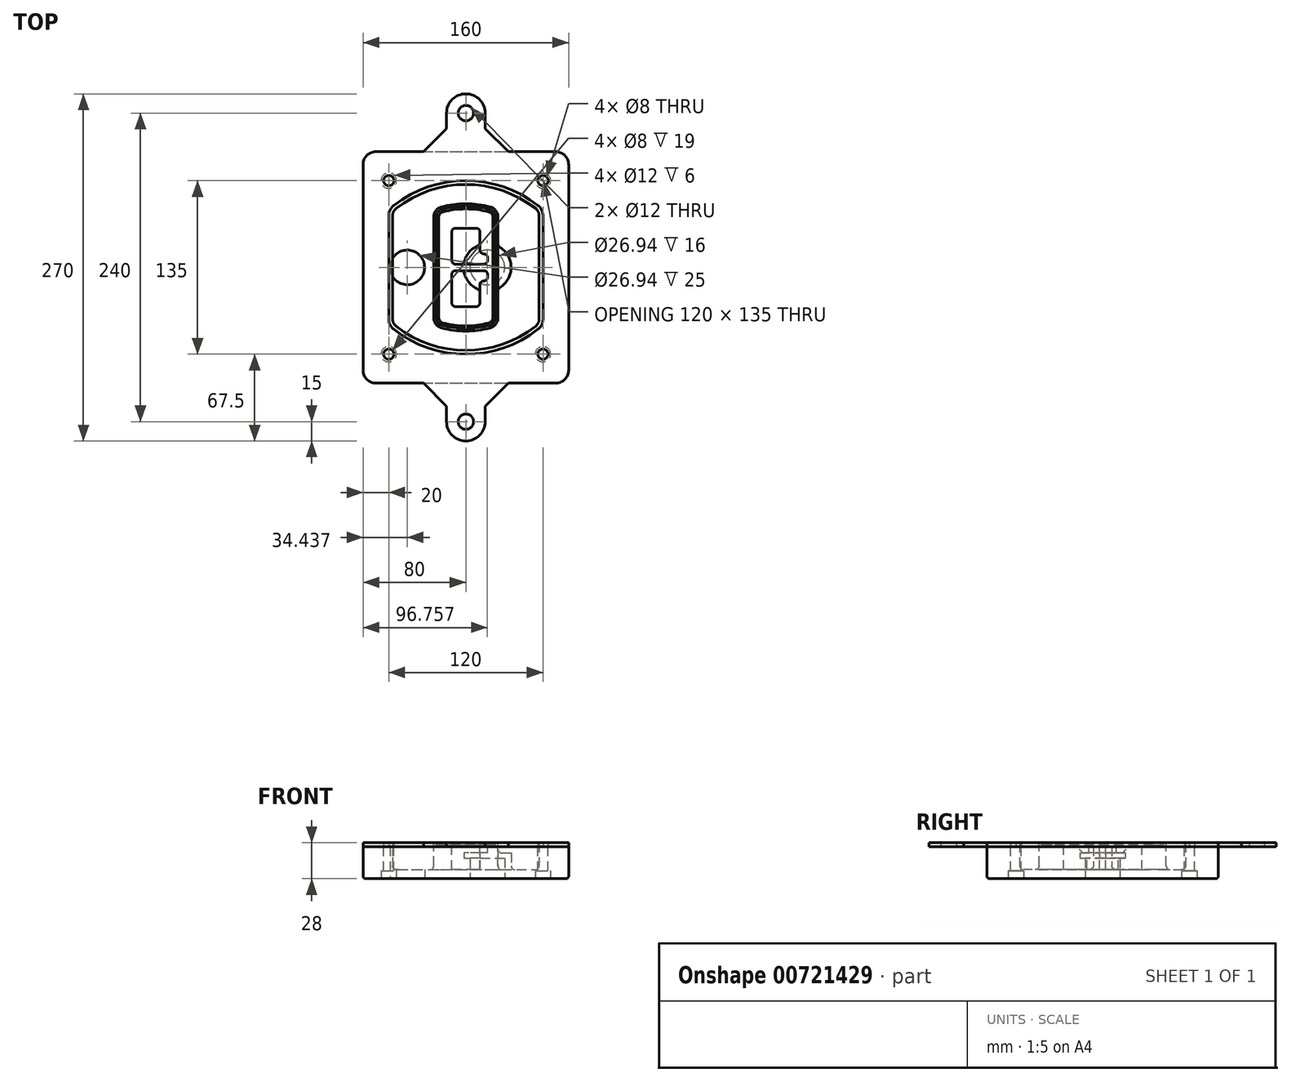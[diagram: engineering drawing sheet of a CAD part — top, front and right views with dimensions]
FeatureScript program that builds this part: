
annotation { "Feature Type Name" : "Feature", "Feature Type Description" : "" }
export const myFeature = defineFeature(function(context is Context, id is Id, definition is map)
    precondition{}
    {
        {
            var Q0;
            Q0=qCreatedBy(makeId("Top.planeOp"),FACE);
            var sketch = newSketch(context, id + "F0", { "sketchPlane" : qUnion([Q0])});
            skPoint(sketch, "E0.rect.middle", {"position": v(0, 0) * mm});
            skLineSegment(sketch, "E1.bottom", {"start": v(-70, -90) * mm, "end": v(70, -90) * mm});
            skLineSegment(sketch, "E1.top", {"start": v(-70, 90) * mm, "end": v(70, 90) * mm});
            skLineSegment(sketch, "E1.left", {"start": v(-80, -80) * mm, "end": v(-80, 80) * mm});
            skLineSegment(sketch, "E1.right", {"start": v(80, -80) * mm, "end": v(80, 80) * mm});
            skLineSegment(sketch, "E2", {"start": v(-80, 90) * mm, "end": v(80, -90) * mm, "construction": true});
            skLineSegment(sketch, "E3", {"start": v(80, 90) * mm, "end": v(-80, -90) * mm, "construction": true});
            skCircle(sketch, "E4", {"center": v(-60, 67.5) * mm, "radius": 4 * mm});
            skCircle(sketch, "E5", {"center": v(60, 67.5) * mm, "radius": 4 * mm});
            skCircle(sketch, "E6", {"center": v(60, -67.5) * mm, "radius": 4 * mm});
            skCircle(sketch, "E7", {"center": v(-60, -67.5) * mm, "radius": 4 * mm});
            skLineSegment(sketch, "E8", {"start": v(-60, 67.5) * mm, "end": v(60, 67.5) * mm, "construction": true});
            skLineSegment(sketch, "E9", {"start": v(60, 67.5) * mm, "end": v(60, -67.5) * mm, "construction": true});
            skLineSegment(sketch, "E10", {"start": v(60, -67.5) * mm, "end": v(-60, -67.5) * mm, "construction": true});
            skLineSegment(sketch, "E11", {"start": v(-60, -67.5) * mm, "end": v(-60, 67.5) * mm, "construction": true});
            skLineSegment(sketch, "E12", {"start": v(-60, 40.3) * mm, "end": v(-60, -40.3) * mm});
            skLineSegment(sketch, "E13", {"start": v(60, 40.3) * mm, "end": v(60, -40.3) * mm});
            skArc(sketch, "E14", {"start": v(56.15, 48.18) * mm, "mid": v(0, 67.5) * mm, "end": v(-56.15, 48.18) * mm});
            skArc(sketch, "E15", {"start": v(-56.15, -48.18) * mm, "mid": v(0, -67.5) * mm, "end": v(56.15, -48.18) * mm});
            skLineSegment(sketch, "E16", {"start": v(-60, 0) * mm, "end": v(60, 0) * mm, "construction": true});
            skPoint(sketch, "E17.visualSharp", {"position": v(-60, -45) * mm});
            skArc(sketch, "E17.filletArc", {"start": v(-60, -40.3) * mm, "mid": v(-58.99, -44.68) * mm, "end": v(-56.15, -48.18) * mm});
            skPoint(sketch, "E18.visualSharp", {"position": v(-60, 45) * mm});
            skArc(sketch, "E18.filletArc", {"start": v(-56.15, 48.18) * mm, "mid": v(-58.99, 44.68) * mm, "end": v(-60, 40.3) * mm});
            skPoint(sketch, "E19.visualSharp", {"position": v(60, 45) * mm});
            skArc(sketch, "E19.filletArc", {"start": v(60, 40.3) * mm, "mid": v(58.99, 44.68) * mm, "end": v(56.15, 48.18) * mm});
            skPoint(sketch, "E20.visualSharp", {"position": v(60, -45) * mm});
            skArc(sketch, "E20.filletArc", {"start": v(56.15, -48.18) * mm, "mid": v(58.99, -44.68) * mm, "end": v(60, -40.3) * mm});
            skPoint(sketch, "E21.visualSharp", {"position": v(-80, 90) * mm});
            skArc(sketch, "E21.filletArc", {"start": v(-70, 90) * mm, "mid": v(-77.07, 87.07) * mm, "end": v(-80, 80) * mm});
            skPoint(sketch, "E22.visualSharp", {"position": v(80, 90) * mm});
            skArc(sketch, "E22.filletArc", {"start": v(80, 80) * mm, "mid": v(77.07, 87.07) * mm, "end": v(70, 90) * mm});
            skPoint(sketch, "E23.visualSharp", {"position": v(80, -90) * mm});
            skArc(sketch, "E23.filletArc", {"start": v(70, -90) * mm, "mid": v(77.07, -87.07) * mm, "end": v(80, -80) * mm});
            skPoint(sketch, "E24.visualSharp", {"position": v(-80, -90) * mm});
            skArc(sketch, "E24.filletArc", {"start": v(-80, -80) * mm, "mid": v(-77.07, -87.07) * mm, "end": v(-70, -90) * mm});
            skArc(sketch, "E25.0", {"start": v(57, 40.3) * mm, "mid": v(56.3, 43.36) * mm, "end": v(54.3, 45.81) * mm});
            skLineSegment(sketch, "E25.1", {"start": v(57, 40.3) * mm, "end": v(57, -40.3) * mm});
            skArc(sketch, "E25.2", {"start": v(54.3, -45.81) * mm, "mid": v(56.3, -43.36) * mm, "end": v(57, -40.3) * mm});
            skArc(sketch, "E25.3", {"start": v(-54.3, -45.81) * mm, "mid": v(0, -64.5) * mm, "end": v(54.3, -45.81) * mm});
            skArc(sketch, "E25.4", {"start": v(-57, -40.3) * mm, "mid": v(-56.3, -43.36) * mm, "end": v(-54.3, -45.81) * mm});
            skArc(sketch, "E25.5", {"start": v(54.3, 45.81) * mm, "mid": v(0, 64.5) * mm, "end": v(-54.3, 45.81) * mm});
            skLineSegment(sketch, "E25.6", {"start": v(-57, 40.3) * mm, "end": v(-57, -40.3) * mm});
            skArc(sketch, "E25.7", {"start": v(-54.3, 45.81) * mm, "mid": v(-56.3, 43.36) * mm, "end": v(-57, 40.3) * mm});
            skArc(sketch, "E26.0", {"start": v(-58.62, 51.33) * mm, "mid": v(-62.58, 46.43) * mm, "end": v(-64, 40.3) * mm});
            skArc(sketch, "E26.1", {"start": v(58.62, 51.33) * mm, "mid": v(0, 71.5) * mm, "end": v(-58.62, 51.33) * mm});
            skArc(sketch, "E26.2", {"start": v(64, 40.3) * mm, "mid": v(62.58, 46.43) * mm, "end": v(58.62, 51.33) * mm});
            skLineSegment(sketch, "E26.3", {"start": v(64, 40.3) * mm, "end": v(64, -40.3) * mm});
            skArc(sketch, "E26.4", {"start": v(58.62, -51.33) * mm, "mid": v(62.58, -46.43) * mm, "end": v(64, -40.3) * mm});
            skLineSegment(sketch, "E26.5", {"start": v(-64, 40.3) * mm, "end": v(-64, -40.3) * mm});
            skArc(sketch, "E26.6", {"start": v(-58.62, -51.33) * mm, "mid": v(0, -71.5) * mm, "end": v(58.62, -51.33) * mm});
            skArc(sketch, "E26.7", {"start": v(-64, -40.3) * mm, "mid": v(-62.58, -46.43) * mm, "end": v(-58.62, -51.33) * mm});
            skSolve(sketch);
        }
        {
            var Q0;
            Q0=makeQuery(id+"F0.imprint","IMPRINT",FACE,{"disambiguationData":[TD([[makeQuery(id+"F0.imprint","IMPRINT",EDGE,{"derivedFrom":sQuery(id+"F0.wireOp",EDGE,"E1.bottom")}),1.0]])]});
            var Q1;
            Q1=makeQuery(id+"F0.imprint","IMPRINT",FACE,{"disambiguationData":[TD([[makeQuery(id+"F0.imprint","IMPRINT",EDGE,{"derivedFrom":sQuery(id+"F0.wireOp",EDGE,"E12")}),1.0]])]});
            var Q2;
            Q2=makeQuery(id+"F0.imprint","IMPRINT",FACE,{"disambiguationData":[TD([[makeQuery(id+"F0.imprint","IMPRINT",EDGE,{"derivedFrom":sQuery(id+"F0.wireOp",EDGE,"E25.0")}),1.0]])]});
            var Q3;
            Q3=makeQuery(id+"F0.imprint","IMPRINT",FACE,{"disambiguationData":[TD([[makeQuery(id+"F0.imprint","IMPRINT",EDGE,{"derivedFrom":sQuery(id+"F0.wireOp",EDGE,"E12")}),-1.0]])]});
            extrude(context, id + "F1", {"entities" : qUnion([Q0, Q1, Q2, Q3]), "oppositeDirection" : true, "depth" : 25 * mm});
        }
        {
            var Q0;
            Q0=makeQuery(id+"F0.imprint","IMPRINT",FACE,{"disambiguationData":[TD([[makeQuery(id+"F0.imprint","IMPRINT",EDGE,{"derivedFrom":sQuery(id+"F0.wireOp",EDGE,"E12")}),1.0]])]});
            extrude(context, id + "F2", {"entities" : qUnion([Q0]), "operationType" : NewBodyOperationType.ADD, "depth" : 3 * mm});
        }
        {
            var Q0;
            Q0=makeQuery(id+"F0.imprint","IMPRINT",FACE,{"disambiguationData":[TD([[makeQuery(id+"F0.imprint","IMPRINT",EDGE,{"derivedFrom":sQuery(id+"F0.wireOp",EDGE,"E25.0")}),1.0]])]});
            extrude(context, id + "F3", {"entities" : qUnion([Q0]), "operationType" : NewBodyOperationType.REMOVE, "oppositeDirection" : true, "depth" : 18 * mm});
        }
        {
            var Q0;
            Q0=makeQuery(id+"F2.opExtrude","CAP_FACE",FACE,{"disambiguationData":[OSD([sQuery(id+"F0.wireOp",EDGE,"E12"),sQuery(id+"F0.wireOp",EDGE,"E13"),sQuery(id+"F0.wireOp",EDGE,"E14"),sQuery(id+"F0.wireOp",EDGE,"E15"),sQuery(id+"F0.wireOp",EDGE,"E17.filletArc"),sQuery(id+"F0.wireOp",EDGE,"E18.filletArc"),sQuery(id+"F0.wireOp",EDGE,"E19.filletArc"),sQuery(id+"F0.wireOp",EDGE,"E20.filletArc"),sQuery(id+"F0.wireOp",EDGE,"E25.0"),sQuery(id+"F0.wireOp",EDGE,"E25.1"),sQuery(id+"F0.wireOp",EDGE,"E25.2"),sQuery(id+"F0.wireOp",EDGE,"E25.3"),sQuery(id+"F0.wireOp",EDGE,"E25.4"),sQuery(id+"F0.wireOp",EDGE,"E25.5"),sQuery(id+"F0.wireOp",EDGE,"E25.6"),sQuery(id+"F0.wireOp",EDGE,"E25.7")])],"isStart":false});
            var sketch = newSketch(context, id + "F4", { "sketchPlane" : qUnion([Q0])});
            skArc(sketch, "E27.0", {"start": v(-19.08, -46.97) * mm, "mid": v(0, -49.5) * mm, "end": v(19.08, -46.97) * mm});
            skArc(sketch, "E28.0", {"start": v(19.08, 46.97) * mm, "mid": v(0, 49.5) * mm, "end": v(-19.08, 46.97) * mm});
            skLineSegment(sketch, "E29", {"start": v(-25, 39.25) * mm, "end": v(-25, -39.25) * mm});
            skLineSegment(sketch, "E30", {"start": v(25, 39.25) * mm, "end": v(25, -39.25) * mm});
            skLineSegment(sketch, "E31", {"start": v(-25, 45.1) * mm, "end": v(25, 45.1) * mm, "construction": true});
            skLineSegment(sketch, "E32", {"start": v(-25, -45.1) * mm, "end": v(25, -45.1) * mm, "construction": true});
            skPoint(sketch, "E33.visualSharp", {"position": v(-25, 45.1) * mm});
            skArc(sketch, "E33.filletArc", {"start": v(-19.08, 46.97) * mm, "mid": v(-23.35, 44.11) * mm, "end": v(-25, 39.25) * mm});
            skPoint(sketch, "E34.visualSharp", {"position": v(25, 45.1) * mm});
            skArc(sketch, "E34.filletArc", {"start": v(25, 39.25) * mm, "mid": v(23.35, 44.11) * mm, "end": v(19.08, 46.97) * mm});
            skPoint(sketch, "E35.visualSharp", {"position": v(25, -45.1) * mm});
            skArc(sketch, "E35.filletArc", {"start": v(19.08, -46.97) * mm, "mid": v(23.35, -44.11) * mm, "end": v(25, -39.25) * mm});
            skPoint(sketch, "E36.visualSharp", {"position": v(-25, -45.1) * mm});
            skArc(sketch, "E36.filletArc", {"start": v(-25, -39.25) * mm, "mid": v(-23.35, -44.11) * mm, "end": v(-19.08, -46.97) * mm});
            skArc(sketch, "E37.0", {"start": v(54.3, 45.81) * mm, "mid": v(0, 64.5) * mm, "end": v(-54.3, 45.81) * mm});
            skArc(sketch, "E37.1", {"start": v(-54.3, 45.81) * mm, "mid": v(-56.3, 43.36) * mm, "end": v(-57, 40.3) * mm});
            skLineSegment(sketch, "E37.2", {"start": v(-57, 40.3) * mm, "end": v(-57, -40.3) * mm});
            skArc(sketch, "E37.3", {"start": v(-57, -40.3) * mm, "mid": v(-56.3, -43.36) * mm, "end": v(-54.3, -45.81) * mm});
            skArc(sketch, "E37.4", {"start": v(-54.3, -45.81) * mm, "mid": v(0, -64.5) * mm, "end": v(54.3, -45.81) * mm});
            skArc(sketch, "E37.5", {"start": v(54.3, -45.81) * mm, "mid": v(56.3, -43.36) * mm, "end": v(57, -40.3) * mm});
            skLineSegment(sketch, "E37.6", {"start": v(57, 40.3) * mm, "end": v(57, -40.3) * mm});
            skArc(sketch, "E37.7", {"start": v(57, 40.3) * mm, "mid": v(56.3, 43.36) * mm, "end": v(54.3, 45.81) * mm});
            skLineSegment(sketch, "E38.0", {"start": v(23, 39.25) * mm, "end": v(23, -39.25) * mm});
            skArc(sketch, "E38.1", {"start": v(18.56, -45.04) * mm, "mid": v(21.76, -42.9) * mm, "end": v(23, -39.25) * mm});
            skArc(sketch, "E38.2", {"start": v(-18.56, -45.04) * mm, "mid": v(0, -47.5) * mm, "end": v(18.56, -45.04) * mm});
            skArc(sketch, "E38.3", {"start": v(-23, -39.25) * mm, "mid": v(-21.76, -42.9) * mm, "end": v(-18.56, -45.04) * mm});
            skLineSegment(sketch, "E38.4", {"start": v(-23, 39.25) * mm, "end": v(-23, -39.25) * mm});
            skArc(sketch, "E38.5", {"start": v(23, 39.25) * mm, "mid": v(21.76, 42.9) * mm, "end": v(18.56, 45.04) * mm});
            skArc(sketch, "E38.6", {"start": v(-18.56, 45.04) * mm, "mid": v(-21.76, 42.9) * mm, "end": v(-23, 39.25) * mm});
            skArc(sketch, "E38.7", {"start": v(18.56, 45.04) * mm, "mid": v(0, 47.5) * mm, "end": v(-18.56, 45.04) * mm});
            skArc(sketch, "E39.0", {"start": v(21, 39.25) * mm, "mid": v(20.18, 41.68) * mm, "end": v(18.04, 43.1) * mm});
            skLineSegment(sketch, "E39.1", {"start": v(21, 39.25) * mm, "end": v(21, -39.25) * mm});
            skArc(sketch, "E39.2", {"start": v(18.04, -43.1) * mm, "mid": v(20.18, -41.68) * mm, "end": v(21, -39.25) * mm});
            skArc(sketch, "E39.3", {"start": v(-18.04, -43.1) * mm, "mid": v(0, -45.5) * mm, "end": v(18.04, -43.1) * mm});
            skArc(sketch, "E39.4", {"start": v(-21, -39.25) * mm, "mid": v(-20.18, -41.68) * mm, "end": v(-18.04, -43.1) * mm});
            skArc(sketch, "E39.5", {"start": v(18.04, 43.1) * mm, "mid": v(0, 45.5) * mm, "end": v(-18.04, 43.1) * mm});
            skLineSegment(sketch, "E39.6", {"start": v(-21, 39.25) * mm, "end": v(-21, -39.25) * mm});
            skArc(sketch, "E39.7", {"start": v(-18.04, 43.1) * mm, "mid": v(-20.18, 41.68) * mm, "end": v(-21, 39.25) * mm});
            skLineSegment(sketch, "E40", {"start": v(-25, 0) * mm, "end": v(25, 0) * mm, "construction": true});
            skLineSegment(sketch, "E41", {"start": v(-11, 5.5) * mm, "end": v(-11, 27.5) * mm});
            skLineSegment(sketch, "E42", {"start": v(-8, 30.5) * mm, "end": v(8, 30.5) * mm});
            skLineSegment(sketch, "E43", {"start": v(11, 27.5) * mm, "end": v(11, 13.5) * mm});
            skLineSegment(sketch, "E44", {"start": v(14, 10.5) * mm, "end": v(14, 10.5) * mm});
            skLineSegment(sketch, "E45", {"start": v(17, 7.5) * mm, "end": v(17, 5.5) * mm});
            skLineSegment(sketch, "E46", {"start": v(14, 2.5) * mm, "end": v(-8, 2.5) * mm});
            skPoint(sketch, "E47.visualSharp", {"position": v(-11, 30.5) * mm});
            skArc(sketch, "E47.filletArc", {"start": v(-8, 30.5) * mm, "mid": v(-10.12, 29.62) * mm, "end": v(-11, 27.5) * mm});
            skPoint(sketch, "E48.visualSharp", {"position": v(11, 30.5) * mm});
            skArc(sketch, "E48.filletArc", {"start": v(11, 27.5) * mm, "mid": v(10.12, 29.62) * mm, "end": v(8, 30.5) * mm});
            skPoint(sketch, "E49.visualSharp", {"position": v(11, 10.5) * mm});
            skArc(sketch, "E49.filletArc", {"start": v(11, 13.5) * mm, "mid": v(11.88, 11.38) * mm, "end": v(14, 10.5) * mm});
            skPoint(sketch, "E50.visualSharp", {"position": v(17, 10.5) * mm});
            skArc(sketch, "E50.filletArc", {"start": v(17, 7.5) * mm, "mid": v(16.12, 9.62) * mm, "end": v(14, 10.5) * mm});
            skPoint(sketch, "E51.visualSharp", {"position": v(17, 2.5) * mm});
            skArc(sketch, "E51.filletArc", {"start": v(14, 2.5) * mm, "mid": v(16.12, 3.38) * mm, "end": v(17, 5.5) * mm});
            skPoint(sketch, "E52.visualSharp", {"position": v(-11, 2.5) * mm});
            skArc(sketch, "E52.filletArc", {"start": v(-11, 5.5) * mm, "mid": v(-10.12, 3.38) * mm, "end": v(-8, 2.5) * mm});
            skLineSegment(sketch, "E53.0.MirrorCS", {"start": v(14, -2.5) * mm, "end": v(-8, -2.5) * mm});
            skArc(sketch, "E54.0.MirrorCS", {"start": v(-11, -5.5) * mm, "mid": v(-10.12, -3.38) * mm, "end": v(-8, -2.5) * mm});
            skLineSegment(sketch, "E55.0.MirrorCS", {"start": v(-11, -5.5) * mm, "end": v(-11, -27.5) * mm});
            skArc(sketch, "E56.0.MirrorCS", {"start": v(-8, -30.5) * mm, "mid": v(-10.12, -29.62) * mm, "end": v(-11, -27.5) * mm});
            skLineSegment(sketch, "E57.0.MirrorCS", {"start": v(-8, -30.5) * mm, "end": v(8, -30.5) * mm});
            skArc(sketch, "E58.0.MirrorCS", {"start": v(11, -27.5) * mm, "mid": v(10.12, -29.62) * mm, "end": v(8, -30.5) * mm});
            skLineSegment(sketch, "E59.0.MirrorCS", {"start": v(11, -27.5) * mm, "end": v(11, -13.5) * mm});
            skArc(sketch, "E60.0.MirrorCS", {"start": v(11, -13.5) * mm, "mid": v(11.88, -11.38) * mm, "end": v(14, -10.5) * mm});
            skArc(sketch, "E61.0.MirrorCS", {"start": v(17, -7.5) * mm, "mid": v(16.12, -9.62) * mm, "end": v(14, -10.5) * mm});
            skLineSegment(sketch, "E62.0.MirrorCS", {"start": v(17, -7.5) * mm, "end": v(17, -5.5) * mm});
            skArc(sketch, "E63.0.MirrorCS", {"start": v(14, -2.5) * mm, "mid": v(16.12, -3.38) * mm, "end": v(17, -5.5) * mm});
            skSolve(sketch);
        }
        {
            var Q0;
            Q0=makeQuery(id+"F4.imprint","IMPRINT",FACE,{"disambiguationData":[TD([[makeQuery(id+"F4.imprint","IMPRINT",EDGE,{"derivedFrom":sQuery(id+"F4.wireOp",EDGE,"E27.0")}),1.0]])]});
            var Q1;
            Q1=makeQuery(id+"F4.imprint","IMPRINT",FACE,{"disambiguationData":[TD([[makeQuery(id+"F4.imprint","IMPRINT",EDGE,{"derivedFrom":sQuery(id+"F4.wireOp",EDGE,"E38.0")}),-1.0]])]});
            var Q2;
            Q2=makeQuery(id+"F4.imprint","IMPRINT",FACE,{"disambiguationData":[TD([[makeQuery(id+"F4.imprint","IMPRINT",EDGE,{"derivedFrom":sQuery(id+"F4.wireOp",EDGE,"E39.0")}),1.0]])]});
            extrude(context, id + "F5", {"entities" : qUnion([Q0, Q1, Q2]), "operationType" : NewBodyOperationType.ADD, "endBound" : BoundingType.UP_TO_NEXT, "oppositeDirection" : true, "depth" : 25 * mm});
        }
        {
            var Q0;
            Q0=makeQuery(id+"F4.imprint","IMPRINT",FACE,{"disambiguationData":[TD([[makeQuery(id+"F4.imprint","IMPRINT",EDGE,{"derivedFrom":sQuery(id+"F4.wireOp",EDGE,"E38.0")}),-1.0]])]});
            extrude(context, id + "F6", {"entities" : qUnion([Q0]), "operationType" : NewBodyOperationType.REMOVE, "oppositeDirection" : true, "depth" : 2 * mm});
        }
        {
            var Q0;
            Q0=makeQuery(id+"F1.opExtrude","CAP_FACE",FACE,{"disambiguationData":[OSD([sQuery(id+"F0.wireOp",EDGE,"E1.bottom"),sQuery(id+"F0.wireOp",EDGE,"E1.top"),sQuery(id+"F0.wireOp",EDGE,"E1.left"),sQuery(id+"F0.wireOp",EDGE,"E1.right"),sQuery(id+"F0.wireOp",EDGE,"E4"),sQuery(id+"F0.wireOp",EDGE,"E5"),sQuery(id+"F0.wireOp",EDGE,"E6"),sQuery(id+"F0.wireOp",EDGE,"E7"),sQuery(id+"F0.wireOp",EDGE,"E21.filletArc"),sQuery(id+"F0.wireOp",EDGE,"E22.filletArc"),sQuery(id+"F0.wireOp",EDGE,"E23.filletArc"),sQuery(id+"F0.wireOp",EDGE,"E24.filletArc")])],"isStart":false});
            var sketch = newSketch(context, id + "F7", { "sketchPlane" : qUnion([Q0])});
            skCircle(sketch, "E64", {"center": v(16.76, 0) * mm, "radius": 13.47 * mm});
            skCircle(sketch, "E65", {"center": v(-45.56, 0) * mm, "radius": 13.47 * mm});
            skLineSegment(sketch, "E66", {"start": v(80, 0) * mm, "end": v(-80, 0) * mm});
            skCircle(sketch, "E67", {"center": v(16.76, 0) * mm, "radius": 18.47 * mm});
            skCircle(sketch, "E68", {"center": v(60, -67.5) * mm, "radius": 6 * mm});
            skCircle(sketch, "E69", {"center": v(-60, -67.5) * mm, "radius": 6 * mm});
            skCircle(sketch, "E70", {"center": v(-60, 67.5) * mm, "radius": 6 * mm});
            skCircle(sketch, "E71", {"center": v(60, 67.5) * mm, "radius": 6 * mm});
            skSolve(sketch);
        }
        {
            var Q0;
            {var subQ1=sQuery(id+"F7.wireOp",EDGE,"E66");var subQ4=sQuery(id+"F7.wireOp",EDGE,"E64");var subQ6=makeQuery(id+"F7.imprint","INTERSECT",VERTEX,{"disambiguationData":[OD(0.0)],"derivedFrom":[subQ4,subQ1]});Q0=makeQuery(id+"F7.imprint","IMPRINT",FACE,{"disambiguationData":[TD([[makeQuery(id+"F7.imprint","IMPRINT",EDGE,{"disambiguationData":[TD([[subQ6,-1.0]])],"derivedFrom":subQ4}),-1.0]])]});}
            var Q1;
            {var subQ0=sQuery(id+"F7.wireOp",EDGE,"E66");var subQ1=sQuery(id+"F7.wireOp",EDGE,"E64");var subQ3=makeQuery(id+"F7.imprint","INTERSECT",VERTEX,{"disambiguationData":[OD(0.0)],"derivedFrom":[subQ1,subQ0]});Q1=makeQuery(id+"F7.imprint","IMPRINT",FACE,{"disambiguationData":[TD([[makeQuery(id+"F7.imprint","IMPRINT",EDGE,{"disambiguationData":[TD([[subQ3,-1.0]])],"derivedFrom":subQ1}),1.0]])]});}
            var Q2;
            {var subQ0=sQuery(id+"F7.wireOp",EDGE,"E66");var subQ1=sQuery(id+"F7.wireOp",EDGE,"E64");var subQ3=makeQuery(id+"F7.imprint","INTERSECT",VERTEX,{"disambiguationData":[OD(0.0)],"derivedFrom":[subQ1,subQ0]});Q2=makeQuery(id+"F7.imprint","IMPRINT",FACE,{"disambiguationData":[TD([[makeQuery(id+"F7.imprint","IMPRINT",EDGE,{"disambiguationData":[TD([[subQ3,1.0]])],"derivedFrom":subQ1}),1.0]])]});}
            var Q3;
            {var subQ1=sQuery(id+"F7.wireOp",EDGE,"E66");var subQ4=sQuery(id+"F7.wireOp",EDGE,"E64");var subQ6=makeQuery(id+"F7.imprint","INTERSECT",VERTEX,{"disambiguationData":[OD(0.0)],"derivedFrom":[subQ4,subQ1]});Q3=makeQuery(id+"F7.imprint","IMPRINT",FACE,{"disambiguationData":[TD([[makeQuery(id+"F7.imprint","IMPRINT",EDGE,{"disambiguationData":[TD([[subQ6,1.0]])],"derivedFrom":subQ4}),-1.0]])]});}
            extrude(context, id + "F8", {"entities" : qUnion([Q0, Q1, Q2, Q3]), "operationType" : NewBodyOperationType.ADD, "oppositeDirection" : true, "depth" : 20 * mm});
        }
        {
            var Q0;
            {var subQ0=sQuery(id+"F7.wireOp",EDGE,"E66");var subQ1=sQuery(id+"F7.wireOp",EDGE,"E64");var subQ3=makeQuery(id+"F7.imprint","INTERSECT",VERTEX,{"disambiguationData":[OD(0.0)],"derivedFrom":[subQ1,subQ0]});Q0=makeQuery(id+"F7.imprint","IMPRINT",FACE,{"disambiguationData":[TD([[makeQuery(id+"F7.imprint","IMPRINT",EDGE,{"disambiguationData":[TD([[subQ3,-1.0]])],"derivedFrom":subQ1}),1.0]])]});}
            var Q1;
            {var subQ0=sQuery(id+"F7.wireOp",EDGE,"E66");var subQ1=sQuery(id+"F7.wireOp",EDGE,"E64");var subQ3=makeQuery(id+"F7.imprint","INTERSECT",VERTEX,{"disambiguationData":[OD(0.0)],"derivedFrom":[subQ1,subQ0]});Q1=makeQuery(id+"F7.imprint","IMPRINT",FACE,{"disambiguationData":[TD([[makeQuery(id+"F7.imprint","IMPRINT",EDGE,{"disambiguationData":[TD([[subQ3,1.0]])],"derivedFrom":subQ1}),1.0]])]});}
            extrude(context, id + "F9", {"entities" : qUnion([Q0, Q1]), "operationType" : NewBodyOperationType.REMOVE, "oppositeDirection" : true, "depth" : 16 * mm});
        }
        {
            var Q0;
            {var subQ0=sQuery(id+"F7.wireOp",EDGE,"E66");var subQ1=sQuery(id+"F7.wireOp",EDGE,"E65");var subQ3=makeQuery(id+"F7.imprint","INTERSECT",VERTEX,{"disambiguationData":[OD(0.0)],"derivedFrom":[subQ1,subQ0]});Q0=makeQuery(id+"F7.imprint","IMPRINT",FACE,{"disambiguationData":[TD([[makeQuery(id+"F7.imprint","IMPRINT",EDGE,{"disambiguationData":[TD([[subQ3,-1.0]])],"derivedFrom":subQ1}),1.0]])]});}
            var Q1;
            {var subQ0=sQuery(id+"F7.wireOp",EDGE,"E66");var subQ1=sQuery(id+"F7.wireOp",EDGE,"E65");var subQ3=makeQuery(id+"F7.imprint","INTERSECT",VERTEX,{"disambiguationData":[OD(0.0)],"derivedFrom":[subQ1,subQ0]});Q1=makeQuery(id+"F7.imprint","IMPRINT",FACE,{"disambiguationData":[TD([[makeQuery(id+"F7.imprint","IMPRINT",EDGE,{"disambiguationData":[TD([[subQ3,1.0]])],"derivedFrom":subQ1}),1.0]])]});}
            extrude(context, id + "F10", {"entities" : qUnion([Q0, Q1]), "operationType" : NewBodyOperationType.REMOVE, "oppositeDirection" : true, "depth" : 25 * mm});
        }
        {
            var Q0;
            Q0=makeQuery(id+"F7.imprint","IMPRINT",FACE,{"disambiguationData":[TD([[makeQuery(id+"F7.imprint","IMPRINT",EDGE,{"derivedFrom":sQuery(id+"F7.wireOp",EDGE,"E68")}),1.0]])]});
            var Q1;
            Q1=makeQuery(id+"F7.imprint","IMPRINT",FACE,{"disambiguationData":[TD([[makeQuery(id+"F7.imprint","IMPRINT",EDGE,{"derivedFrom":makeQuery(id+"F1.opExtrude","CAP_EDGE",EDGE,{"disambiguationData":[OSD([sQuery(id+"F0.wireOp",EDGE,"E5")])],"isStart":false})}),-1.0]])]});
            var Q2;
            Q2=makeQuery(id+"F7.imprint","IMPRINT",FACE,{"disambiguationData":[TD([[makeQuery(id+"F7.imprint","IMPRINT",EDGE,{"derivedFrom":sQuery(id+"F7.wireOp",EDGE,"E69")}),1.0]])]});
            var Q3;
            Q3=makeQuery(id+"F7.imprint","IMPRINT",FACE,{"disambiguationData":[TD([[makeQuery(id+"F7.imprint","IMPRINT",EDGE,{"derivedFrom":makeQuery(id+"F1.opExtrude","CAP_EDGE",EDGE,{"disambiguationData":[OSD([sQuery(id+"F0.wireOp",EDGE,"E4")])],"isStart":false})}),-1.0]])]});
            var Q4;
            Q4=makeQuery(id+"F7.imprint","IMPRINT",FACE,{"disambiguationData":[TD([[makeQuery(id+"F7.imprint","IMPRINT",EDGE,{"derivedFrom":sQuery(id+"F7.wireOp",EDGE,"E70")}),1.0]])]});
            var Q5;
            Q5=makeQuery(id+"F7.imprint","IMPRINT",FACE,{"disambiguationData":[TD([[makeQuery(id+"F7.imprint","IMPRINT",EDGE,{"derivedFrom":makeQuery(id+"F1.opExtrude","CAP_EDGE",EDGE,{"disambiguationData":[OSD([sQuery(id+"F0.wireOp",EDGE,"E7")])],"isStart":false})}),-1.0]])]});
            var Q6;
            Q6=makeQuery(id+"F7.imprint","IMPRINT",FACE,{"disambiguationData":[TD([[makeQuery(id+"F7.imprint","IMPRINT",EDGE,{"derivedFrom":sQuery(id+"F7.wireOp",EDGE,"E71")}),1.0]])]});
            var Q7;
            Q7=makeQuery(id+"F7.imprint","IMPRINT",FACE,{"disambiguationData":[TD([[makeQuery(id+"F7.imprint","IMPRINT",EDGE,{"derivedFrom":makeQuery(id+"F1.opExtrude","CAP_EDGE",EDGE,{"disambiguationData":[OSD([sQuery(id+"F0.wireOp",EDGE,"E6")])],"isStart":false})}),-1.0]])]});
            extrude(context, id + "F11", {"entities" : qUnion([Q0, Q1, Q2, Q3, Q4, Q5, Q6, Q7]), "operationType" : NewBodyOperationType.REMOVE, "oppositeDirection" : true, "depth" : 6 * mm});
        }
        {
            var Q0;
            Q0=makeQuery(id+"F9.boolean.opBoolean","COPY",FACE,{"derivedFrom":makeQuery(id+"F9.opExtrude","CAP_FACE",FACE,{"disambiguationData":[OSD([sQuery(id+"F7.wireOp",EDGE,"E64")])],"isStart":false})});
            var sketch = newSketch(context, id + "F12", { "sketchPlane" : qUnion([Q0])});
            skArc(sketch, "E72.0", {"start": v(11, 17.55) * mm, "mid": v(2.57, 11.82) * mm, "end": v(-1.54, 2.5) * mm});
            skArc(sketch, "E72.1", {"start": v(-1.54, -2.5) * mm, "mid": v(2.57, -11.82) * mm, "end": v(11, -17.55) * mm});
            skLineSegment(sketch, "E73", {"start": v(-1.54, -2.5) * mm, "end": v(14, -2.5) * mm});
            skLineSegment(sketch, "E74.0", {"start": v(14, 2.5) * mm, "end": v(-1.54, 2.5) * mm});
            skArc(sketch, "E74.1", {"start": v(14, 2.5) * mm, "mid": v(16.12, 3.38) * mm, "end": v(17, 5.5) * mm});
            skLineSegment(sketch, "E74.2", {"start": v(17, 7.5) * mm, "end": v(17, 5.5) * mm});
            skArc(sketch, "E74.3", {"start": v(17, 7.5) * mm, "mid": v(16.12, 9.62) * mm, "end": v(14, 10.5) * mm});
            skArc(sketch, "E74.4", {"start": v(11, 13.5) * mm, "mid": v(11.88, 11.38) * mm, "end": v(14, 10.5) * mm});
            skLineSegment(sketch, "E74.5", {"start": v(11, 17.55) * mm, "end": v(11, 13.5) * mm});
            skLineSegment(sketch, "E74.7", {"start": v(14, -2.5) * mm, "end": v(-1.54, -2.5) * mm});
            skArc(sketch, "E74.8", {"start": v(14, -2.5) * mm, "mid": v(16.12, -3.38) * mm, "end": v(17, -5.5) * mm});
            skLineSegment(sketch, "E74.9", {"start": v(17, -7.5) * mm, "end": v(17, -5.5) * mm});
            skArc(sketch, "E74.10", {"start": v(17, -7.5) * mm, "mid": v(16.12, -9.62) * mm, "end": v(14, -10.5) * mm});
            skArc(sketch, "E74.11", {"start": v(11, -13.5) * mm, "mid": v(11.88, -11.38) * mm, "end": v(14, -10.5) * mm});
            skLineSegment(sketch, "E74.12", {"start": v(11, -17.55) * mm, "end": v(11, -13.5) * mm});
            skPoint(sketch, "E75.orphan", {"position": v(11, -27.5) * mm});
            skPoint(sketch, "E76.orphan", {"position": v(-8, -2.5) * mm});
            skPoint(sketch, "E77.orphan", {"position": v(-8, 2.5) * mm});
            skPoint(sketch, "E78.orphan", {"position": v(11, 27.5) * mm});
            skSolve(sketch);
        }
        {
            var Q0;
            {var subQ7=sQuery(id+"F12.wireOp",EDGE,"E72.0");var subQ14=sQuery(id+"F12.wireOp",EDGE,"E72.1");var subQ16=sQuery(id+"F12.wireOp",EDGE,"E74.1");var subQ18=sQuery(id+"F12.wireOp",EDGE,"E74.8");Q0=qUnion([makeQuery(id+"F12.imprint","IMPRINT",FACE,{"disambiguationData":[TD([[makeQuery(id+"F12.imprint","IMPRINT",EDGE,{"derivedFrom":subQ7}),1.0]])]}),makeQuery(id+"F12.imprint","IMPRINT",FACE,{"disambiguationData":[TD([[makeQuery(id+"F12.imprint","IMPRINT",EDGE,{"derivedFrom":subQ14}),1.0]])]}),makeQuery(id+"F12.imprint","IMPRINT",FACE,{"disambiguationData":[TD([[makeQuery(id+"F12.imprint","IMPRINT",EDGE,{"derivedFrom":subQ16}),1.0]])]}),makeQuery(id+"F12.imprint","IMPRINT",FACE,{"disambiguationData":[TD([[makeQuery(id+"F12.imprint","IMPRINT",EDGE,{"derivedFrom":subQ18}),-1.0]])]})]);}
            var Q1;
            Q1=makeQuery(id+"F5.boolean.opBoolean","SPLIT",FACE,{"disambiguationData":[TD([makeQuery(id+"F5.opExtrude","SWEPT_FACE",FACE,{"disambiguationData":[OSD([sQuery(id+"F4.wireOp",EDGE,"E41")])]})])],"derivedFrom":makeQuery(id+"F3.boolean.opBoolean","COPY",FACE,{"derivedFrom":makeQuery(id+"F3.opExtrude","CAP_FACE",FACE,{"disambiguationData":[OSD([sQuery(id+"F0.wireOp",EDGE,"E25.0"),sQuery(id+"F0.wireOp",EDGE,"E25.1"),sQuery(id+"F0.wireOp",EDGE,"E25.2"),sQuery(id+"F0.wireOp",EDGE,"E25.3"),sQuery(id+"F0.wireOp",EDGE,"E25.4"),sQuery(id+"F0.wireOp",EDGE,"E25.5"),sQuery(id+"F0.wireOp",EDGE,"E25.6"),sQuery(id+"F0.wireOp",EDGE,"E25.7")])],"isStart":false})})});
            extrude(context, id + "F13", {"entities" : qUnion([Q0]), "operationType" : NewBodyOperationType.REMOVE, "endBound" : BoundingType.UP_TO_SURFACE, "endBoundEntityFace" : qUnion([Q1]), "depth" : 25 * mm});
        }
        {
            var Q0;
            Q0=makeQuery(id+"F3.boolean.opBoolean","COPY",EDGE,{"derivedFrom":makeQuery(id+"F3.opExtrude","CAP_EDGE",EDGE,{"disambiguationData":[OSD([sQuery(id+"F0.wireOp",EDGE,"E25.6")])],"isStart":false})});
            var Q1;
            Q1=makeQuery(id+"F8.boolean.opBoolean","INTERSECT",EDGE,{"derivedFrom":[makeQuery(id+"F5.opExtrude","SWEPT_FACE",FACE,{"disambiguationData":[OSD([sQuery(id+"F4.wireOp",EDGE,"E30")])]}),makeQuery(id+"F8.opExtrude","CAP_FACE",FACE,{"disambiguationData":[OSD([sQuery(id+"F7.wireOp",EDGE,"E67")])],"isStart":false})]});
            var Q2;
            Q2=makeQuery(id+"F8.boolean.opBoolean","INTERSECT",EDGE,{"disambiguationData":[OD(1.0)],"derivedFrom":[makeQuery(id+"F5.opExtrude","SWEPT_FACE",FACE,{"disambiguationData":[OSD([sQuery(id+"F4.wireOp",EDGE,"E30")])]}),makeQuery(id+"F8.opExtrude","SWEPT_FACE",FACE,{"disambiguationData":[OSD([sQuery(id+"F7.wireOp",EDGE,"E67")])]})]});
            var Q3;
            {var subQ0=sQuery(id+"F4.wireOp",EDGE,"E30");Q3=makeQuery(id+"F8.boolean.opBoolean","SPLIT",EDGE,{"disambiguationData":[TD([makeQuery(id+"F5.opExtrude","SWEPT_FACE",FACE,{"disambiguationData":[OSD([sQuery(id+"F4.wireOp",EDGE,"E35.filletArc")])]})])],"derivedFrom":makeQuery(id+"F5.opExtrude","CAP_EDGE",EDGE,{"disambiguationData":[OSD([subQ0])],"isStart":false})});}
            var Q4;
            {var subQ0=sQuery(id+"F0.wireOp",EDGE,"E25.7");var subQ1=sQuery(id+"F0.wireOp",EDGE,"E25.1");var subQ2=sQuery(id+"F0.wireOp",EDGE,"E25.6");var subQ3=sQuery(id+"F0.wireOp",EDGE,"E25.5");var subQ4=sQuery(id+"F0.wireOp",EDGE,"E25.4");var subQ5=sQuery(id+"F0.wireOp",EDGE,"E25.0");var subQ6=sQuery(id+"F0.wireOp",EDGE,"E25.2");var subQ7=sQuery(id+"F0.wireOp",EDGE,"E25.3");Q4=makeQuery(id+"F8.boolean.opBoolean","INTERSECT",EDGE,{"derivedFrom":[makeQuery(id+"F5.boolean.opBoolean","SPLIT",FACE,{"disambiguationData":[TD([makeQuery(id+"F2.opExtrude","SWEPT_FACE",FACE,{"disambiguationData":[OSD([subQ5])]})])],"derivedFrom":makeQuery(id+"F3.boolean.opBoolean","COPY",FACE,{"derivedFrom":makeQuery(id+"F3.opExtrude","CAP_FACE",FACE,{"disambiguationData":[OSD([subQ5,subQ1,subQ6,subQ7,subQ4,subQ3,subQ2,subQ0])],"isStart":false})})}),makeQuery(id+"F8.opExtrude","SWEPT_FACE",FACE,{"disambiguationData":[OSD([sQuery(id+"F7.wireOp",EDGE,"E67")])]})]});}
            var Q5;
            Q5=makeQuery(id+"F8.boolean.opBoolean","INTERSECT",EDGE,{"disambiguationData":[OD(0.0)],"derivedFrom":[makeQuery(id+"F5.opExtrude","SWEPT_FACE",FACE,{"disambiguationData":[OSD([sQuery(id+"F4.wireOp",EDGE,"E30")])]}),makeQuery(id+"F8.opExtrude","SWEPT_FACE",FACE,{"disambiguationData":[OSD([sQuery(id+"F7.wireOp",EDGE,"E67")])]})]});
            fillet(context, id + "F14", {"entities" : qUnion([Q0, Q1, Q2, Q3, Q4, Q5]), "radius" : 3 * mm, "tangentPropagation" : true, "allowEdgeOverflow" : false});
        }
        {
            var Q0;
            Q0=makeQuery(id+"F1.opExtrude","CAP_EDGE",EDGE,{"disambiguationData":[OSD([sQuery(id+"F0.wireOp",EDGE,"E1.bottom")])],"isStart":false});
            fillet(context, id + "F15", {"entities" : qUnion([Q0]), "radius" : 2 * mm, "tangentPropagation" : true, "allowEdgeOverflow" : false});
        }
        {
            var Q0;
            {var subQ0=sQuery(id+"F0.wireOp",EDGE,"E21.filletArc");var subQ1=sQuery(id+"F0.wireOp",EDGE,"E7");var subQ2=sQuery(id+"F0.wireOp",EDGE,"E6");var subQ3=sQuery(id+"F0.wireOp",EDGE,"E5");var subQ4=sQuery(id+"F0.wireOp",EDGE,"E4");var subQ5=sQuery(id+"F0.wireOp",EDGE,"E22.filletArc");var subQ6=sQuery(id+"F0.wireOp",EDGE,"E1.bottom");var subQ7=sQuery(id+"F0.wireOp",EDGE,"E1.right");var subQ8=sQuery(id+"F0.wireOp",EDGE,"E1.top");var subQ9=sQuery(id+"F0.wireOp",EDGE,"E1.left");var subQ10=sQuery(id+"F0.wireOp",EDGE,"E23.filletArc");var subQ11=sQuery(id+"F0.wireOp",EDGE,"E24.filletArc");Q0=makeQuery(id+"F2.boolean.opBoolean","SPLIT",FACE,{"disambiguationData":[TD([makeQuery(id+"F1.opExtrude","SWEPT_FACE",FACE,{"disambiguationData":[OSD([subQ6])]})])],"derivedFrom":makeQuery(id+"F1.opExtrude","CAP_FACE",FACE,{"disambiguationData":[OSD([subQ6,subQ8,subQ9,subQ7,subQ4,subQ3,subQ2,subQ1,subQ0,subQ5,subQ10,subQ11])],"isStart":true})});}
            var sketch = newSketch(context, id + "F16", { "sketchPlane" : qUnion([Q0])});
            skLineSegment(sketch, "E79.0", {"start": v(-80, -80) * mm, "end": v(-80, 80) * mm});
            skArc(sketch, "E79.1", {"start": v(-70, 90) * mm, "mid": v(-77.07, 87.07) * mm, "end": v(-80, 80) * mm});
            skLineSegment(sketch, "E79.2", {"start": v(-70, 90) * mm, "end": v(70, 90) * mm});
            skArc(sketch, "E79.3", {"start": v(80, 80) * mm, "mid": v(77.07, 87.07) * mm, "end": v(70, 90) * mm});
            skLineSegment(sketch, "E79.4", {"start": v(80, -80) * mm, "end": v(80, 80) * mm});
            skArc(sketch, "E79.5", {"start": v(70, -90) * mm, "mid": v(77.07, -87.07) * mm, "end": v(80, -80) * mm});
            skLineSegment(sketch, "E79.6", {"start": v(-70, -90) * mm, "end": v(70, -90) * mm});
            skArc(sketch, "E79.7", {"start": v(-80, -80) * mm, "mid": v(-77.07, -87.07) * mm, "end": v(-70, -90) * mm});
            skArc(sketch, "E79.8", {"start": v(-56.15, -48.18) * mm, "mid": v(0, -67.5) * mm, "end": v(56.15, -48.18) * mm});
            skLineSegment(sketch, "E79.9", {"start": v(-60, 40.3) * mm, "end": v(-60, -40.3) * mm});
            skArc(sketch, "E79.10", {"start": v(56.15, 48.18) * mm, "mid": v(0, 67.5) * mm, "end": v(-56.15, 48.18) * mm});
            skLineSegment(sketch, "E79.11", {"start": v(60, 40.3) * mm, "end": v(60, -40.3) * mm});
            skArc(sketch, "E79.12", {"start": v(60, 40.3) * mm, "mid": v(58.99, 44.68) * mm, "end": v(56.15, 48.18) * mm});
            skArc(sketch, "E79.13", {"start": v(-56.15, 48.18) * mm, "mid": v(-58.99, 44.68) * mm, "end": v(-60, 40.3) * mm});
            skArc(sketch, "E79.14", {"start": v(-60, -40.3) * mm, "mid": v(-58.99, -44.68) * mm, "end": v(-56.15, -48.18) * mm});
            skArc(sketch, "E79.15", {"start": v(56.15, -48.18) * mm, "mid": v(58.99, -44.68) * mm, "end": v(60, -40.3) * mm});
            skCircle(sketch, "E79.16", {"center": v(60, 67.5) * mm, "radius": 4 * mm});
            skCircle(sketch, "E79.17", {"center": v(60, -67.5) * mm, "radius": 4 * mm});
            skCircle(sketch, "E79.18", {"center": v(-60, -67.5) * mm, "radius": 4 * mm});
            skCircle(sketch, "E79.19", {"center": v(-60, 67.5) * mm, "radius": 4 * mm});
            skLineSegment(sketch, "E80", {"start": v(0, 23.75) * mm, "end": v(0, 120) * mm, "construction": true});
            skLineSegment(sketch, "E81", {"start": v(-33, 90) * mm, "end": v(-15, 108) * mm});
            skLineSegment(sketch, "E82", {"start": v(-15, 108) * mm, "end": v(-15, 120) * mm});
            skLineSegment(sketch, "E83", {"start": v(33, 90) * mm, "end": v(15, 108) * mm});
            skLineSegment(sketch, "E84", {"start": v(15, 108) * mm, "end": v(15, 120) * mm});
            skArc(sketch, "E85", {"start": v(-15, 120) * mm, "mid": v(0, 135) * mm, "end": v(15, 120) * mm});
            skCircle(sketch, "E86", {"center": v(0, 120) * mm, "radius": 2.12 * mm});
            skCircle(sketch, "E87", {"center": v(0, 120) * mm, "radius": 6 * mm});
            skArc(sketch, "E88.MirrorCS", {"start": v(15, 120) * mm, "mid": v(0, 135) * mm, "end": v(-15, 120) * mm});
            skLineSegment(sketch, "E89.MirrorCS", {"start": v(70, 90) * mm, "end": v(-70, 90) * mm});
            skArc(sketch, "E90.MirrorCS", {"start": v(70, 90) * mm, "mid": v(77.07, 87.07) * mm, "end": v(80, 80) * mm});
            skLineSegment(sketch, "E91", {"start": v(-80, 0) * mm, "end": v(80, 0) * mm, "construction": true});
            skCircle(sketch, "E92.MirrorC", {"center": v(0, -120) * mm, "radius": 2.12 * mm});
            skLineSegment(sketch, "E93.MirrorCS", {"start": v(-15, -108) * mm, "end": v(-15, -120) * mm});
            skLineSegment(sketch, "E94.MirrorCS", {"start": v(15, -108) * mm, "end": v(15, -120) * mm});
            skCircle(sketch, "E95.MirrorC", {"center": v(0, -120) * mm, "radius": 6 * mm});
            skLineSegment(sketch, "E96.MirrorCS", {"start": v(-33, -90) * mm, "end": v(-15, -108) * mm});
            skLineSegment(sketch, "E97.MirrorCS", {"start": v(33, -90) * mm, "end": v(15, -108) * mm});
            skArc(sketch, "E98.MirrorCS", {"start": v(-15, -120) * mm, "mid": v(0, -135) * mm, "end": v(15, -120) * mm});
            skArc(sketch, "E99.MirrorCS", {"start": v(15, -120) * mm, "mid": v(0, -135) * mm, "end": v(-15, -120) * mm});
            skLineSegment(sketch, "E100.MirrorCS", {"start": v(0, -23.75) * mm, "end": v(0, -120) * mm, "construction": true});
            skSolve(sketch);
        }
        {
            var Q0;
            Q0 = qSketchRegion(id + "F16", true);
            var Q1;
            Q1=makeQuery(id+"F2.opExtrude","CAP_FACE",FACE,{"disambiguationData":[OSD([sQuery(id+"F0.wireOp",EDGE,"E12"),sQuery(id+"F0.wireOp",EDGE,"E13"),sQuery(id+"F0.wireOp",EDGE,"E14"),sQuery(id+"F0.wireOp",EDGE,"E15"),sQuery(id+"F0.wireOp",EDGE,"E17.filletArc"),sQuery(id+"F0.wireOp",EDGE,"E18.filletArc"),sQuery(id+"F0.wireOp",EDGE,"E19.filletArc"),sQuery(id+"F0.wireOp",EDGE,"E20.filletArc"),sQuery(id+"F0.wireOp",EDGE,"E25.0"),sQuery(id+"F0.wireOp",EDGE,"E25.1"),sQuery(id+"F0.wireOp",EDGE,"E25.2"),sQuery(id+"F0.wireOp",EDGE,"E25.3"),sQuery(id+"F0.wireOp",EDGE,"E25.4"),sQuery(id+"F0.wireOp",EDGE,"E25.5"),sQuery(id+"F0.wireOp",EDGE,"E25.6"),sQuery(id+"F0.wireOp",EDGE,"E25.7")])],"isStart":false});
            extrude(context, id + "F17", {"entities" : qUnion([Q0]), "endBound" : BoundingType.UP_TO_SURFACE, "depth" : 25 * mm, "endBoundEntityFace" : qUnion([Q1]), "offsetDistance" : 25 * mm});
        }
    });
